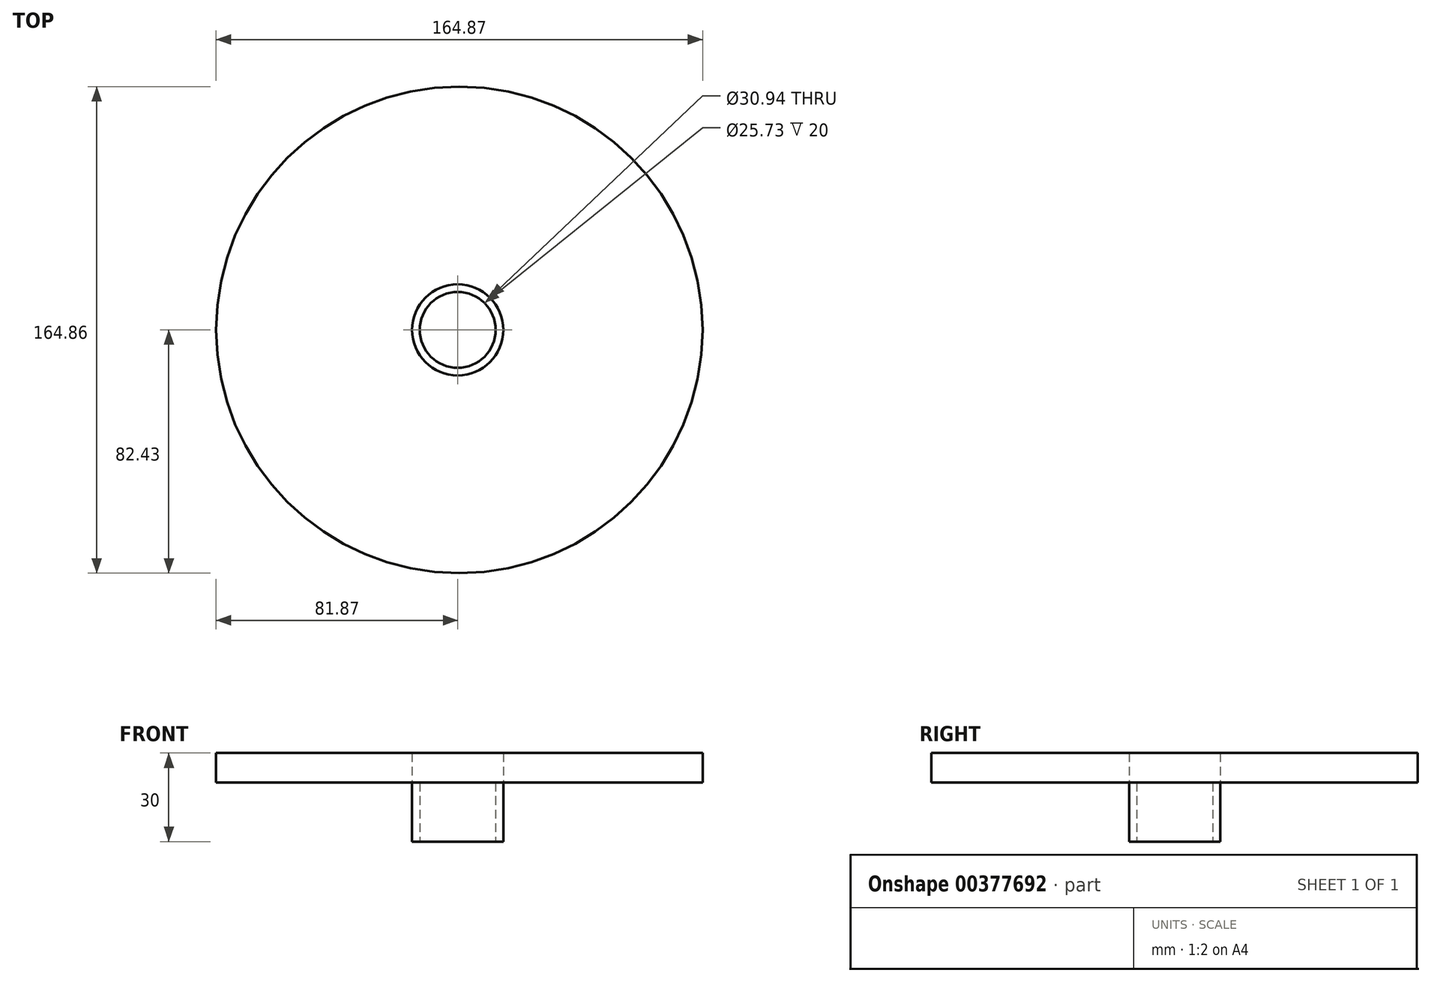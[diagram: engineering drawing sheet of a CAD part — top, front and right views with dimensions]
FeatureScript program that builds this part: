
annotation { "Feature Type Name" : "Feature", "Feature Type Description" : "" }
export const myFeature = defineFeature(function(context is Context, id is Id, definition is map)
    precondition{}
    {
        {
            var Q0;
            Q0=qCreatedBy(makeId("Top.planeOp"),FACE);
            var sketch = newSketch(context, id + "F0", { "sketchPlane" : qUnion([Q0])});
            skCircle(sketch, "E0", {"center": v(0, 0) * mm, "radius": 15.47 * mm});
            skCircle(sketch, "E1", {"center": v(0, 0) * mm, "radius": 12.87 * mm});
            skSolve(sketch);
        }
        {
            var Q0;
            Q0=makeQuery(id+"F0.imprint","IMPRINT",FACE,{"disambiguationData":[TD([[makeQuery(id+"F0.imprint","IMPRINT",EDGE,{"derivedFrom":sQuery(id+"F0.wireOp",EDGE,"E0")}),1.0]])]});
            extrude(context, id + "F1", {"entities" : qUnion([Q0]), "depth" : 20 * mm});
        }
        {
            var Q0;
            Q0=makeQuery(id+"F1.opExtrude","CAP_FACE",FACE,{"disambiguationData":[OSD([sQuery(id+"F0.wireOp",EDGE,"E0"),sQuery(id+"F0.wireOp",EDGE,"E1")])],"isStart":false});
            var sketch = newSketch(context, id + "F2", { "sketchPlane" : qUnion([Q0])});
            skCircle(sketch, "E2", {"center": v(0.56, 0) * mm, "radius": 82.43 * mm});
            skSolve(sketch);
        }
        {
            var Q0;
            Q0=makeQuery(id+"F2.imprint","IMPRINT",FACE,{"disambiguationData":[TD([[makeQuery(id+"F2.imprint","IMPRINT",EDGE,{"derivedFrom":sQuery(id+"F2.wireOp",EDGE,"E2")}),1.0]])]});
            extrude(context, id + "F3", {"entities" : qUnion([Q0]), "depth" : 10 * mm});
        }
    });
